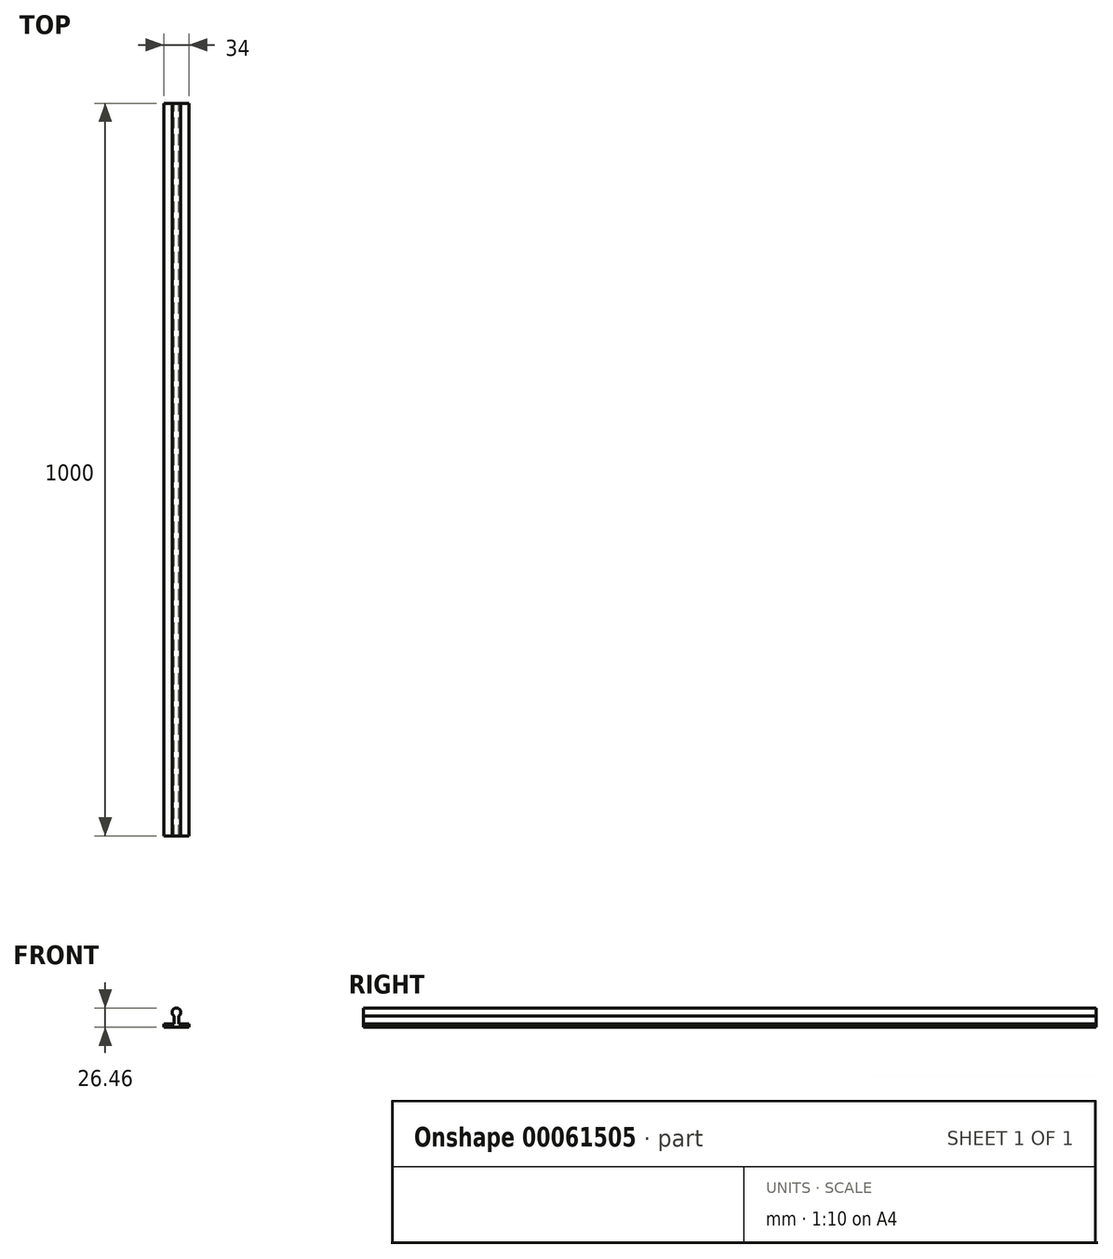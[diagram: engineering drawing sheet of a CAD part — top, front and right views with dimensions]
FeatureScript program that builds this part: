
annotation { "Feature Type Name" : "Feature", "Feature Type Description" : "" }
export const myFeature = defineFeature(function(context is Context, id is Id, definition is map)
    precondition{}
    {
        {
            var Q0;
            Q0=qCreatedBy(makeId("Front.planeOp"),FACE);
            var sketch = newSketch(context, id + "F0", { "sketchPlane" : qUnion([Q0])});
            skCircle(sketch, "E0", {"center": v(0, 0) * mm, "radius": 6 * mm});
            skLineSegment(sketch, "E1", {"start": v(3, 0) * mm, "end": v(3, -15.96) * mm});
            skLineSegment(sketch, "E2", {"start": v(3, -15.96) * mm, "end": v(-17, -15.96) * mm});
            skLineSegment(sketch, "E3", {"start": v(-17, -15.96) * mm, "end": v(-17, -20.46) * mm});
            skLineSegment(sketch, "E4", {"start": v(-17, -20.46) * mm, "end": v(0, -20.46) * mm});
            skLineSegment(sketch, "E5.MirrorCS", {"start": v(17, -20.46) * mm, "end": v(0, -20.46) * mm});
            skLineSegment(sketch, "E6.MirrorCS", {"start": v(17, -15.96) * mm, "end": v(17, -20.46) * mm});
            skLineSegment(sketch, "E7.MirrorCS", {"start": v(-3, -15.96) * mm, "end": v(17, -15.96) * mm});
            skLineSegment(sketch, "E8.MirrorCS", {"start": v(-3, 0) * mm, "end": v(-3, -15.96) * mm});
            skSolve(sketch);
        }
        {
            var Q0;
            {var subQ0=sQuery(id+"F0.wireOp",EDGE,"E0");var subQ1=makeQuery(id+"F0.imprint","INTERSECT",VERTEX,{"derivedFrom":[subQ0,sQuery(id+"F0.wireOp",EDGE,"E1")]});Q0=makeQuery(id+"F0.imprint","IMPRINT",FACE,{"disambiguationData":[TD([[makeQuery(id+"F0.imprint","IMPRINT",EDGE,{"disambiguationData":[TD([[subQ1,1.0]])],"derivedFrom":subQ0}),1.0]])]});}
            var Q1;
            {var subQ0=sQuery(id+"F0.wireOp",EDGE,"E2");Q1=makeQuery(id+"F0.imprint","IMPRINT",FACE,{"disambiguationData":[TD([[makeQuery(id+"F0.imprint","IMPRINT",EDGE,{"derivedFrom":subQ0}),1.0]])]});}
            var Q2;
            {var subQ0=sQuery(id+"F0.wireOp",EDGE,"E1");var subQ1=sQuery(id+"F0.wireOp",EDGE,"E0");var subQ2=makeQuery(id+"F0.imprint","INTERSECT",VERTEX,{"derivedFrom":[subQ1,subQ0]});Q2=makeQuery(id+"F0.imprint","IMPRINT",FACE,{"disambiguationData":[TD([[makeQuery(id+"F0.imprint","IMPRINT",EDGE,{"disambiguationData":[TD([[subQ2,1.0]])],"derivedFrom":subQ1}),-1.0]])]});}
            extrude(context, id + "F1", {"entities" : qUnion([Q0, Q1, Q2]), "depth" : 1000 * mm, "symmetric" : true});
        }
    });
